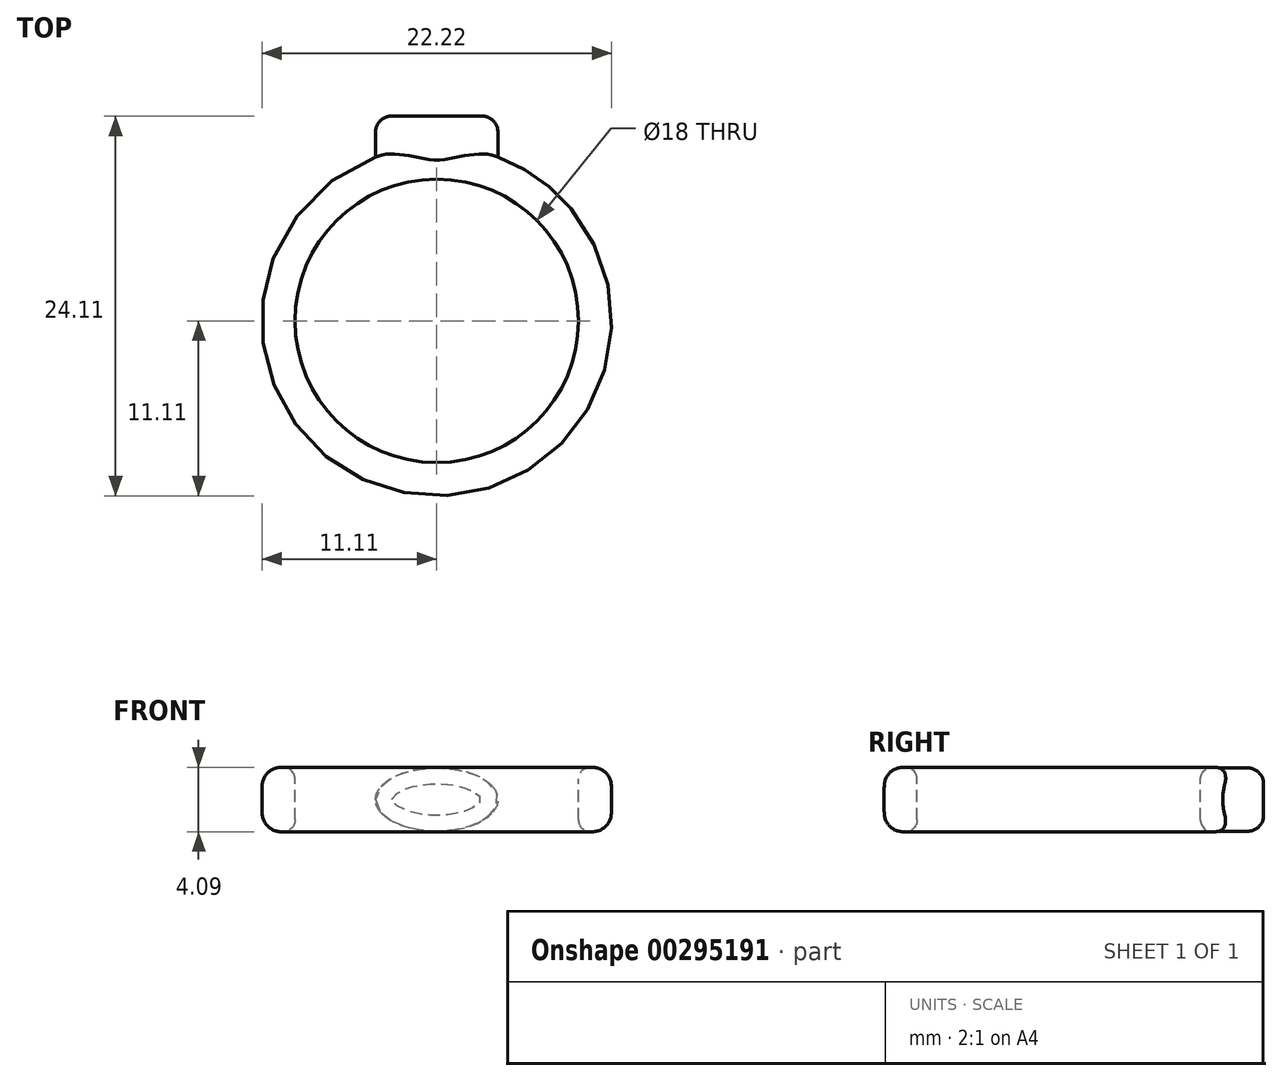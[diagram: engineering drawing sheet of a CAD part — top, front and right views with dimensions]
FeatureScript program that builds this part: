
annotation { "Feature Type Name" : "Feature", "Feature Type Description" : "" }
export const myFeature = defineFeature(function(context is Context, id is Id, definition is map)
    precondition{}
    {
        {
            var Q0;
            Q0=qCreatedBy(makeId("Top.planeOp"),FACE);
            var sketch = newSketch(context, id + "F0", { "sketchPlane" : qUnion([Q0])});
            skCircle(sketch, "E0", {"center": v(0, 0) * mm, "radius": 9 * mm});
            skSolve(sketch);
        }
        {
            var Q0;
            Q0=qSketchRegion(id+"F0",true);
            extrude(context, id + "F1", {"entities" : qUnion([Q0]), "depth" : 5 * mm});
        }
        {
            var Q0;
            Q0=qCreatedBy(makeId("Front.planeOp"),FACE);
            var sketch = newSketch(context, id + "F2", { "sketchPlane" : qUnion([Q0])});
            skLineSegment(sketch, "E1", {"start": v(-9, 0) * mm, "end": v(-9, 4.09) * mm});
            skLineSegment(sketch, "E2", {"start": v(-9, 4.09) * mm, "end": v(-11, 4.09) * mm});
            skLineSegment(sketch, "E3", {"start": v(-9, 0) * mm, "end": v(-11, 0) * mm});
            skEllipticalArc(sketch, "E4", {});
            const initialGuessF2  = {"E4": [-0.009, 0.002044621467089722, 0, 1, 0.006460695860003162, 0.0021083652104055594, 1.248789600770858, 1.8928030528189346]};
            skSetInitialGuess(sketch, initialGuessF2);
            skSolve(sketch);
        }
        {
            var Q0;
            Q0=makeQuery(id+"F2.imprint","IMPRINT",FACE,{"disambiguationData":[TD([[makeQuery(id+"F2.imprint","IMPRINT",EDGE,{"derivedFrom":sQuery(id+"F2.wireOp",EDGE,"E1")}),1.0]])]});
            var Q1;
            Q1=makeQuery(id+"F1.opExtrude","SWEPT_FACE",FACE,{"disambiguationData":[OSD([sQuery(id+"F0.wireOp",EDGE,"E0")])]});
            revolve(context, id + "F3", {"entities" : qUnion([Q0]), "axis" : qUnion([Q1]), "revolveType" : RevolveType.FULL});
        }
        {
            var Q0;
            Q0=makeQuery(id+"F3.opRevolve","SWEPT_EDGE",EDGE,{"disambiguationData":[OSD([sQuery(id+"F2.wireOp",EDGE,"E2"),sQuery(id+"F2.wireOp",EDGE,"E4")])]});
            var Q1;
            Q1=makeQuery(id+"F3.opRevolve","SWEPT_EDGE",EDGE,{"disambiguationData":[OSD([sQuery(id+"F2.wireOp",EDGE,"E3"),sQuery(id+"F2.wireOp",EDGE,"E4")])]});
            fillet(context, id + "F4", {"entities" : qUnion([Q0, Q1]), "radius" : 1.2 * mm, "tangentPropagation" : true, "allowEdgeOverflow" : false});
        }
        {
            var Q0;
            Q0=makeQuery(id+"F3.opRevolve","SWEPT_EDGE",EDGE,{"disambiguationData":[OSD([sQuery(id+"F2.wireOp",EDGE,"E1"),sQuery(id+"F2.wireOp",EDGE,"E3")])]});
            var Q1;
            Q1=makeQuery(id+"F3.opRevolve","SWEPT_EDGE",EDGE,{"disambiguationData":[OSD([sQuery(id+"F2.wireOp",EDGE,"E1"),sQuery(id+"F2.wireOp",EDGE,"E2")])]});
            fillet(context, id + "F5", {"entities" : qUnion([Q0, Q1]), "radius" : .75 * mm, "tangentPropagation" : true, "allowEdgeOverflow" : false});
        }
        {
            var Q0;
            Q0=makeQuery(id+"F1.opExtrude","SWEPT_BODY",BODY,{"disambiguationData":[OSD([sQuery(id+"F0.wireOp",EDGE,"E0")])]});
            deleteBodies(context, id + "F6", {"entities" : qUnion([Q0])});
        }
        {
            var Q0;
            Q0=qCreatedBy(makeId("Front.planeOp"),FACE);
            cPlane(context, id + "F7", {"entities" : qUnion([Q0]), "cplaneType" : CPlaneType.OFFSET, "offset" : 10 * mm, "oppositeDirection" : true, "width" : 150 * mm, "height" : 150 * mm});
        }
        {
            var Q0;
            Q0=qCreatedBy(id+"F7.planeOp",FACE);
            var sketch = newSketch(context, id + "F8", { "sketchPlane" : qUnion([Q0])});
            skEllipse(sketch, "E5", {"center": v(0, 2.04) * mm, "majorRadius": 3.89 * mm, "minorRadius": 2 * mm, "majorAxis": v(-1, 0)});
            skSolve(sketch);
        }
        {
            var Q0;
            Q0=qSketchRegion(id+"F8",true);
            extrude(context, id + "F9", {"entities" : qUnion([Q0]), "operationType" : NewBodyOperationType.ADD, "oppositeDirection" : true, "depth" : 3 * mm});
        }
        {
            var Q0;
            Q0=makeQuery(id+"F9.opExtrude","CAP_EDGE",EDGE,{"disambiguationData":[OSD([sQuery(id+"F8.wireOp",EDGE,"E5")])],"isStart":false});
            fillet(context, id + "F10", {"entities" : qUnion([Q0]), "radius" : 1 * mm, "tangentPropagation" : true, "allowEdgeOverflow" : false});
        }
    });
